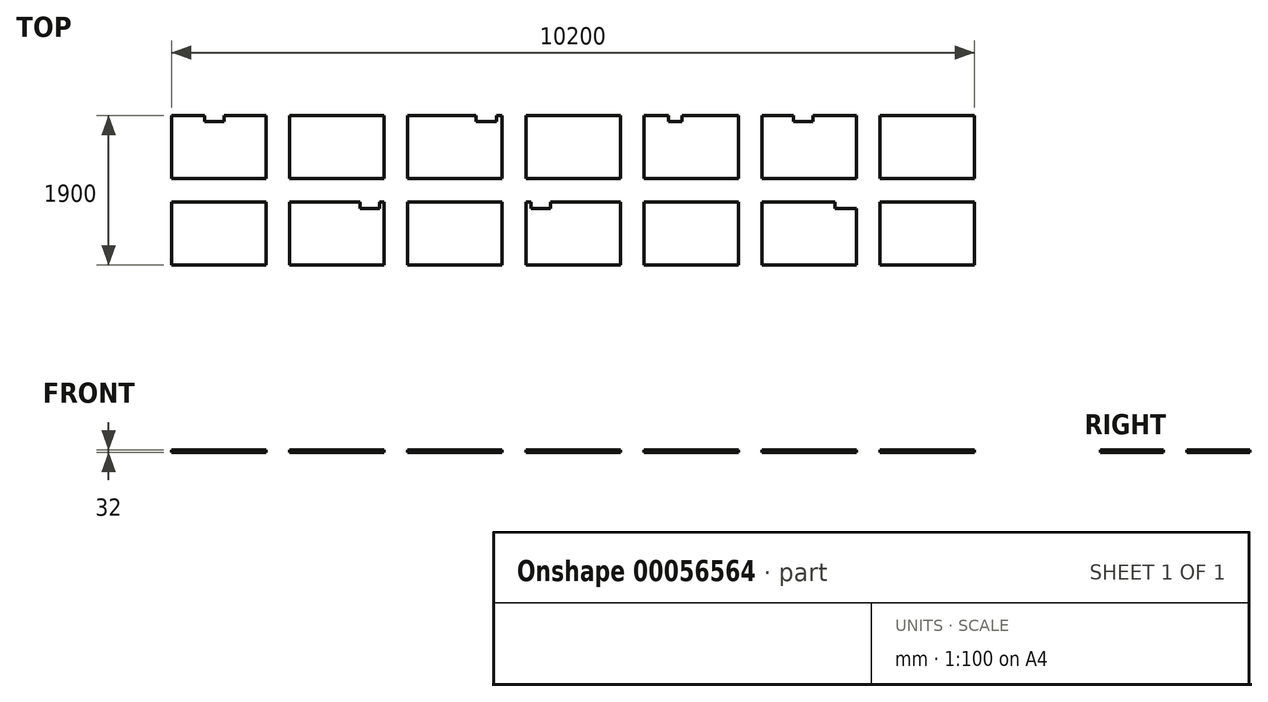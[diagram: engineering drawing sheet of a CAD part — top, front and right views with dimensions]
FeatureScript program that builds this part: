
annotation { "Feature Type Name" : "Feature", "Feature Type Description" : "" }
export const myFeature = defineFeature(function(context is Context, id is Id, definition is map)
    precondition{}
    {
        {
            var Q0;
            Q0=qCreatedBy(makeId("Top.planeOp"),FACE);
            var sketch = newSketch(context, id + "F0", { "sketchPlane" : qUnion([Q0])});
            skLineSegment(sketch, "E0.bottom", {"start": v(-851.18, -2.78) * mm, "end": v(-431.18, -2.78) * mm});
            skLineSegment(sketch, "E0.top", {"start": v(-851.18, -802.78) * mm, "end": v(348.82, -802.78) * mm});
            skLineSegment(sketch, "E0.left", {"start": v(-851.18, -2.78) * mm, "end": v(-851.18, -802.78) * mm});
            skLineSegment(sketch, "E0.right", {"start": v(348.82, -2.78) * mm, "end": v(348.82, -802.78) * mm});
            skLineSegment(sketch, "E1.right", {"start": v(1848.82, -2.78) * mm, "end": v(1848.82, -802.78) * mm});
            skLineSegment(sketch, "E1.left", {"start": v(648.82, -2.78) * mm, "end": v(648.82, -802.78) * mm});
            skLineSegment(sketch, "E1.top", {"start": v(648.82, -802.78) * mm, "end": v(1848.82, -802.78) * mm});
            skLineSegment(sketch, "E1.bottom", {"start": v(648.82, -2.78) * mm, "end": v(1848.82, -2.78) * mm});
            skLineSegment(sketch, "E2.right", {"start": v(3348.82, -2.78) * mm, "end": v(3348.82, -802.78) * mm});
            skLineSegment(sketch, "E2.left", {"start": v(2148.82, -2.78) * mm, "end": v(2148.82, -802.78) * mm});
            skLineSegment(sketch, "E2.top", {"start": v(2148.82, -802.78) * mm, "end": v(3348.82, -802.78) * mm});
            skLineSegment(sketch, "E2.bottom", {"start": v(2148.82, -2.78) * mm, "end": v(3018.82, -2.78) * mm});
            skLineSegment(sketch, "E3.right", {"start": v(4848.82, -2.78) * mm, "end": v(4848.82, -802.78) * mm});
            skLineSegment(sketch, "E3.left", {"start": v(3648.82, -2.78) * mm, "end": v(3648.82, -802.78) * mm});
            skLineSegment(sketch, "E3.top", {"start": v(3648.82, -802.78) * mm, "end": v(4848.82, -802.78) * mm});
            skLineSegment(sketch, "E3.bottom", {"start": v(3648.82, -2.78) * mm, "end": v(4848.82, -2.78) * mm});
            skLineSegment(sketch, "E4.right", {"start": v(6348.82, -2.78) * mm, "end": v(6348.82, -802.78) * mm});
            skLineSegment(sketch, "E4.left", {"start": v(5148.82, -2.78) * mm, "end": v(5148.82, -802.78) * mm});
            skLineSegment(sketch, "E4.top", {"start": v(5148.82, -802.78) * mm, "end": v(6348.82, -802.78) * mm});
            skLineSegment(sketch, "E4.bottom", {"start": v(5148.82, -2.78) * mm, "end": v(5458.82, -2.78) * mm});
            skLineSegment(sketch, "E5.right", {"start": v(7848.82, -2.78) * mm, "end": v(7848.82, -802.78) * mm});
            skLineSegment(sketch, "E5.left", {"start": v(6648.82, -2.78) * mm, "end": v(6648.82, -802.78) * mm});
            skLineSegment(sketch, "E5.top", {"start": v(6648.82, -802.78) * mm, "end": v(7848.82, -802.78) * mm});
            skLineSegment(sketch, "E5.bottom", {"start": v(6648.82, -2.78) * mm, "end": v(7048.82, -2.78) * mm});
            skLineSegment(sketch, "E6.right", {"start": v(9348.82, -2.78) * mm, "end": v(9348.82, -802.78) * mm});
            skLineSegment(sketch, "E6.left", {"start": v(8148.82, -2.78) * mm, "end": v(8148.82, -802.78) * mm});
            skLineSegment(sketch, "E6.top", {"start": v(8148.82, -802.78) * mm, "end": v(9348.82, -802.78) * mm});
            skLineSegment(sketch, "E6.bottom", {"start": v(8148.82, -2.78) * mm, "end": v(9348.82, -2.78) * mm});
            skLineSegment(sketch, "E7.right", {"start": v(348.82, -1102.78) * mm, "end": v(348.82, -1902.78) * mm});
            skLineSegment(sketch, "E7.left", {"start": v(-851.18, -1102.78) * mm, "end": v(-851.18, -1902.78) * mm});
            skLineSegment(sketch, "E7.top", {"start": v(-851.18, -1902.78) * mm, "end": v(348.82, -1902.78) * mm});
            skLineSegment(sketch, "E7.bottom", {"start": v(-851.18, -1102.78) * mm, "end": v(348.82, -1102.78) * mm});
            skLineSegment(sketch, "E8.right", {"start": v(1848.82, -1102.78) * mm, "end": v(1848.82, -1902.78) * mm});
            skLineSegment(sketch, "E8.left", {"start": v(648.82, -1102.78) * mm, "end": v(648.82, -1902.78) * mm});
            skLineSegment(sketch, "E8.top", {"start": v(648.82, -1902.78) * mm, "end": v(1848.82, -1902.78) * mm});
            skLineSegment(sketch, "E8.bottom", {"start": v(648.82, -1102.78) * mm, "end": v(1543.82, -1102.78) * mm});
            skLineSegment(sketch, "E9.right", {"start": v(3348.82, -1102.78) * mm, "end": v(3348.82, -1902.78) * mm});
            skLineSegment(sketch, "E9.left", {"start": v(2148.82, -1102.78) * mm, "end": v(2148.82, -1902.78) * mm});
            skLineSegment(sketch, "E9.top", {"start": v(2148.82, -1902.78) * mm, "end": v(3348.82, -1902.78) * mm});
            skLineSegment(sketch, "E9.bottom", {"start": v(2148.82, -1102.78) * mm, "end": v(3348.82, -1102.78) * mm});
            skLineSegment(sketch, "E10.right", {"start": v(4848.82, -1102.78) * mm, "end": v(4848.82, -1902.78) * mm});
            skLineSegment(sketch, "E10.left", {"start": v(3648.82, -1102.78) * mm, "end": v(3648.82, -1902.78) * mm});
            skLineSegment(sketch, "E10.top", {"start": v(3648.82, -1902.78) * mm, "end": v(4848.82, -1902.78) * mm});
            skLineSegment(sketch, "E10.bottom", {"start": v(3648.82, -1102.78) * mm, "end": v(3713.82, -1102.78) * mm});
            skLineSegment(sketch, "E11.right", {"start": v(6348.82, -1102.78) * mm, "end": v(6348.82, -1902.78) * mm});
            skLineSegment(sketch, "E11.left", {"start": v(5148.82, -1102.78) * mm, "end": v(5148.82, -1902.78) * mm});
            skLineSegment(sketch, "E11.top", {"start": v(5148.82, -1902.78) * mm, "end": v(6348.82, -1902.78) * mm});
            skLineSegment(sketch, "E11.bottom", {"start": v(5148.82, -1102.78) * mm, "end": v(6348.82, -1102.78) * mm});
            skLineSegment(sketch, "E12.right", {"start": v(7848.82, -1182.78) * mm, "end": v(7848.82, -1902.78) * mm});
            skLineSegment(sketch, "E12.left", {"start": v(6648.82, -1102.78) * mm, "end": v(6648.82, -1902.78) * mm});
            skLineSegment(sketch, "E12.top", {"start": v(6648.82, -1902.78) * mm, "end": v(7848.82, -1902.78) * mm});
            skLineSegment(sketch, "E12.bottom", {"start": v(6648.82, -1102.78) * mm, "end": v(7578.82, -1102.78) * mm});
            skLineSegment(sketch, "E13.right", {"start": v(9348.82, -1102.78) * mm, "end": v(9348.82, -1902.78) * mm});
            skLineSegment(sketch, "E13.left", {"start": v(8148.82, -1102.78) * mm, "end": v(8148.82, -1902.78) * mm});
            skLineSegment(sketch, "E13.top", {"start": v(8148.82, -1902.78) * mm, "end": v(9348.82, -1902.78) * mm});
            skLineSegment(sketch, "E13.bottom", {"start": v(8148.82, -1102.78) * mm, "end": v(9348.82, -1102.78) * mm});
            skLineSegment(sketch, "E14.top", {"start": v(-431.18, -82.78) * mm, "end": v(-181.18, -82.78) * mm});
            skLineSegment(sketch, "E14.left", {"start": v(-431.18, -2.78) * mm, "end": v(-431.18, -82.78) * mm});
            skLineSegment(sketch, "E14.right", {"start": v(-181.18, -2.78) * mm, "end": v(-181.18, -82.78) * mm});
            skLineSegment(sketch, "E15.trimOffspring", {"start": v(-181.18, -2.78) * mm, "end": v(348.82, -2.78) * mm});
            skLineSegment(sketch, "E16.top", {"start": v(3018.82, -82.78) * mm, "end": v(3278.82, -82.78) * mm});
            skLineSegment(sketch, "E16.left", {"start": v(3018.82, -2.78) * mm, "end": v(3018.82, -82.78) * mm});
            skLineSegment(sketch, "E16.right", {"start": v(3278.82, -2.78) * mm, "end": v(3278.82, -82.78) * mm});
            skLineSegment(sketch, "E17.trimOffspring", {"start": v(3278.82, -2.78) * mm, "end": v(3348.82, -2.78) * mm});
            skLineSegment(sketch, "E18.top", {"start": v(5458.82, -82.78) * mm, "end": v(5633.82, -82.78) * mm});
            skLineSegment(sketch, "E18.left", {"start": v(5458.82, -2.78) * mm, "end": v(5458.82, -82.78) * mm});
            skLineSegment(sketch, "E18.right", {"start": v(5633.82, -2.78) * mm, "end": v(5633.82, -82.78) * mm});
            skLineSegment(sketch, "E19.trimOffspring", {"start": v(5633.82, -2.78) * mm, "end": v(6348.82, -2.78) * mm});
            skLineSegment(sketch, "E20.top", {"start": v(7048.82, -82.78) * mm, "end": v(7298.82, -82.78) * mm});
            skLineSegment(sketch, "E20.left", {"start": v(7048.82, -2.78) * mm, "end": v(7048.82, -82.78) * mm});
            skLineSegment(sketch, "E20.right", {"start": v(7298.82, -2.78) * mm, "end": v(7298.82, -82.78) * mm});
            skLineSegment(sketch, "E21.trimOffspring", {"start": v(7298.82, -2.78) * mm, "end": v(7848.82, -2.78) * mm});
            skLineSegment(sketch, "E22.top", {"start": v(1543.82, -1182.78) * mm, "end": v(1793.82, -1182.78) * mm});
            skLineSegment(sketch, "E22.left", {"start": v(1543.82, -1102.78) * mm, "end": v(1543.82, -1182.78) * mm});
            skLineSegment(sketch, "E22.right", {"start": v(1793.82, -1102.78) * mm, "end": v(1793.82, -1182.78) * mm});
            skLineSegment(sketch, "E23.trimOffspring", {"start": v(1793.82, -1102.78) * mm, "end": v(1848.82, -1102.78) * mm});
            skLineSegment(sketch, "E24.top", {"start": v(3713.82, -1182.78) * mm, "end": v(3963.82, -1182.78) * mm});
            skLineSegment(sketch, "E24.left", {"start": v(3713.82, -1102.78) * mm, "end": v(3713.82, -1182.78) * mm});
            skLineSegment(sketch, "E24.right", {"start": v(3963.82, -1102.78) * mm, "end": v(3963.82, -1182.78) * mm});
            skLineSegment(sketch, "E25.trimOffspring", {"start": v(3963.82, -1102.78) * mm, "end": v(4848.82, -1102.78) * mm});
            skLineSegment(sketch, "E26.top", {"start": v(7578.82, -1182.78) * mm, "end": v(7848.82, -1182.78) * mm});
            skLineSegment(sketch, "E26.left", {"start": v(7578.82, -1102.78) * mm, "end": v(7578.82, -1182.78) * mm});
            skSolve(sketch);
        }
        {
            var Q0;
            Q0 = qSketchRegion(id + "F0", true);
            extrude(context, id + "F1", {"entities" : qUnion([Q0]), "depth" : 32 * mm});
        }
    });
